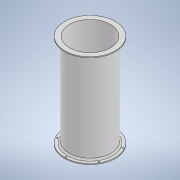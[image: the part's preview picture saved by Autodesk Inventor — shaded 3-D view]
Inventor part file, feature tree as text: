
AUTODESK INVENTOR PART (.ipt)
format: ipt  version: 2020 (Build 240168000, 168)  size: 155,136 bytes
history: native  units: mm
features: revolve x1, hole x1, sketch x1, projected_geometry x1
ambient origin geometry x8: Origin, YZ Plane, XZ Plane, XY Plane, X Axis, Y Axis, Z Axis, Center Point
bodies: Solid1 (feature_tree)
feature tree (4):
  revolve  "Revolution1"  Angle=90.0deg
  hole  "Hole1"  [1 undecoded]
  sketch  "Sketch2"  dims[d0=300.0mm d3=90.0deg d5=81.5mm d6=2.0mm d7=9.0mm d8=5.0mm d9=45.0deg d10=16.0mm d11=3.0mm d12=3.0mm d13=9.0mm d14=45.0deg d15=5.0mm d16=4.5mm d17=8.0mm d18=60.0mm d20=360.0deg d22=4.5mm d23=10.0mm d24=9.4mm d25=2.0mm d26=90.0deg d27=13.0mm d28=20.594885mm d29=4.5mm]
  projected_geometry  "Projected Loop1"
note: 1 required parameter value undecoded (feature->parameter linkage not recoverable at this tier; creation-order binding heuristic only, values carry confidence <= 0.55)
